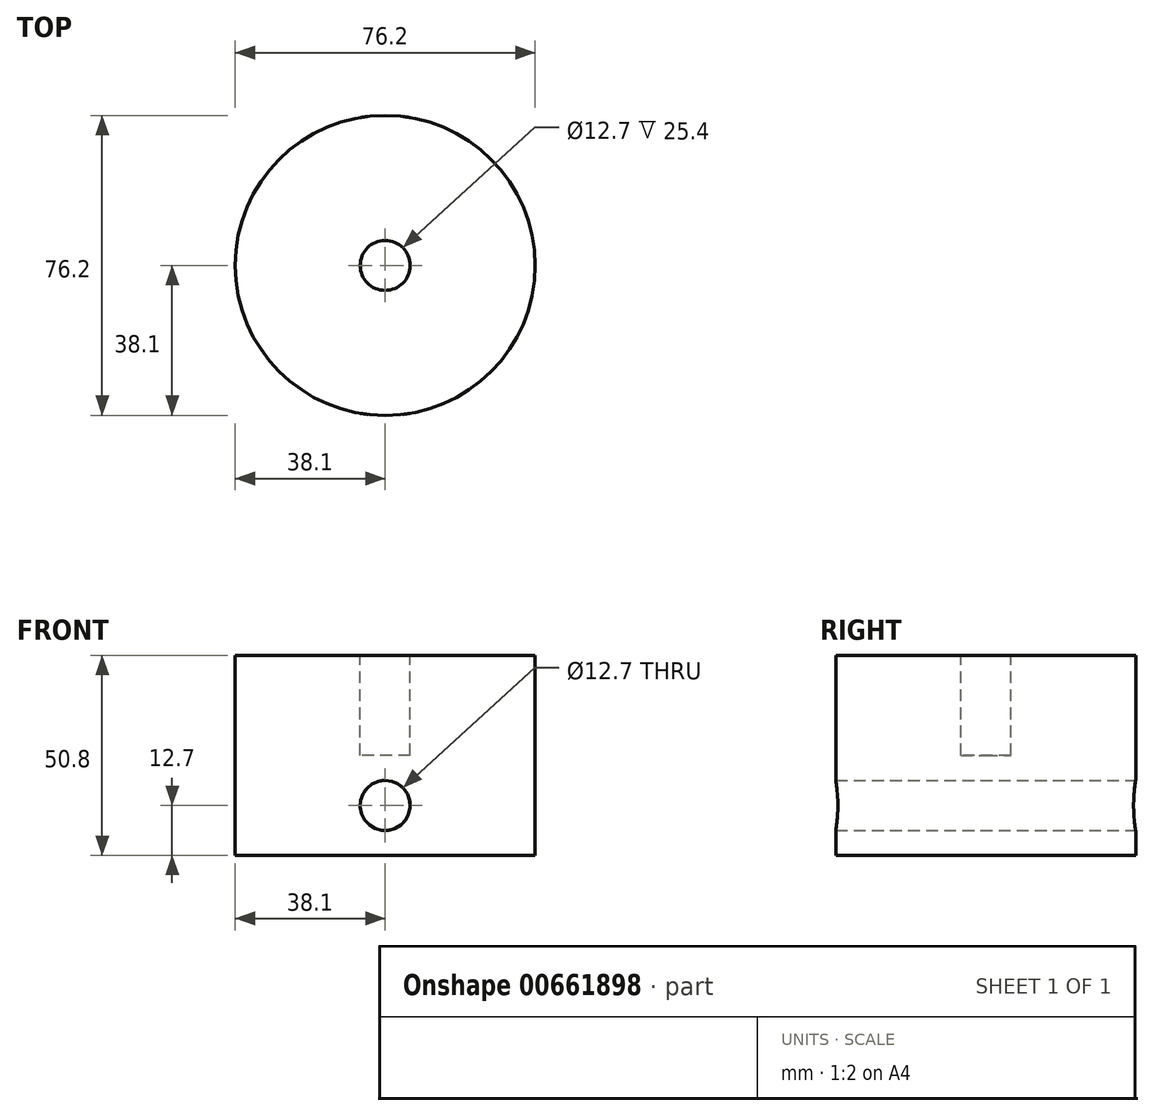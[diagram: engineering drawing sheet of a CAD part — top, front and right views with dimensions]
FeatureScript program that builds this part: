
annotation { "Feature Type Name" : "Feature", "Feature Type Description" : "" }
export const myFeature = defineFeature(function(context is Context, id is Id, definition is map)
    precondition{}
    {
        {
            var Q0;
            Q0=qCreatedBy(makeId("Top.planeOp"),FACE);
            var sketch = newSketch(context, id + "F0", { "sketchPlane" : qUnion([Q0])});
            skCircle(sketch, "E0", {"center": v(0, 0) * mm, "radius": 38.1 * mm});
            skSolve(sketch);
        }
        {
            var Q0;
            Q0 = qSketchRegion(id + "F0", true);
            extrude(context, id + "F1", {"entities" : qUnion([Q0]), "depth" : 50.8 * mm, "offsetDistance" : 25.4 * mm});
        }
        {
            var Q0;
            Q0=qCreatedBy(makeId("Front.planeOp"),FACE);
            var sketch = newSketch(context, id + "F2", { "sketchPlane" : qUnion([Q0])});
            skPoint(sketch, "E1", {"position": v(0, 12.7) * mm});
            skSolve(sketch);
        }
        {
            var Q0;
            Q0=sQuery(id+"F2.wireOp",VERTEX,"E1");
            var Q1;
            Q1=makeQuery(id+"F1.opExtrude","SWEPT_BODY",BODY,{"disambiguationData":[OSD([sQuery(id+"F0.wireOp",EDGE,"E0")])]});
            hole(context, id + "F3", {"style" : HoleStyle.SIMPLE, "endStyle" : HoleEndStyle.BLIND, "oppositeDirection" : true, "holeDiameter" : 12.7 * mm, "majorDiameter" : 6.35 * mm, "holeDepth" : 101.6 * mm, "isTappedThrough" : true, "tappedDepth" : 12.7 * mm, "tapClearance" : 3, "startFromSketch" : true, "locations" : qUnion([Q0]), "scope" : qUnion([Q1])});
        }
        {
            var Q0;
            Q0=sQuery(id+"F2.wireOp",VERTEX,"E1");
            var Q1;
            Q1=makeQuery(id+"F1.opExtrude","SWEPT_BODY",BODY,{"disambiguationData":[OSD([sQuery(id+"F0.wireOp",EDGE,"E0")])]});
            hole(context, id + "F4", {"style" : HoleStyle.SIMPLE, "endStyle" : HoleEndStyle.BLIND, "holeDiameter" : 12.7 * mm, "majorDiameter" : 6.35 * mm, "holeDepth" : 101.6 * mm, "isTappedThrough" : true, "tappedDepth" : 12.7 * mm, "tapClearance" : 3, "startFromSketch" : true, "locations" : qUnion([Q0]), "scope" : qUnion([Q1])});
        }
        {
            var Q0;
            Q0=makeQuery(id+"F1.opExtrude","CAP_FACE",FACE,{"disambiguationData":[OSD([sQuery(id+"F0.wireOp",EDGE,"E0")])],"isStart":false});
            var sketch = newSketch(context, id + "F5", { "sketchPlane" : qUnion([Q0])});
            skCircle(sketch, "E2", {"center": v(0, 0) * mm, "radius": 6.35 * mm});
            skSolve(sketch);
        }
        {
            var Q0;
            Q0=makeQuery(id+"F5.imprint","IMPRINT",FACE,{"disambiguationData":[TD([[makeQuery(id+"F5.imprint","IMPRINT",EDGE,{"derivedFrom":sQuery(id+"F5.wireOp",EDGE,"E2")}),1.0]])]});
            extrude(context, id + "F6", {"entities" : qUnion([Q0]), "operationType" : NewBodyOperationType.REMOVE, "oppositeDirection" : true, "depth" : 25.4 * mm, "offsetDistance" : 25.4 * mm});
        }
    });
